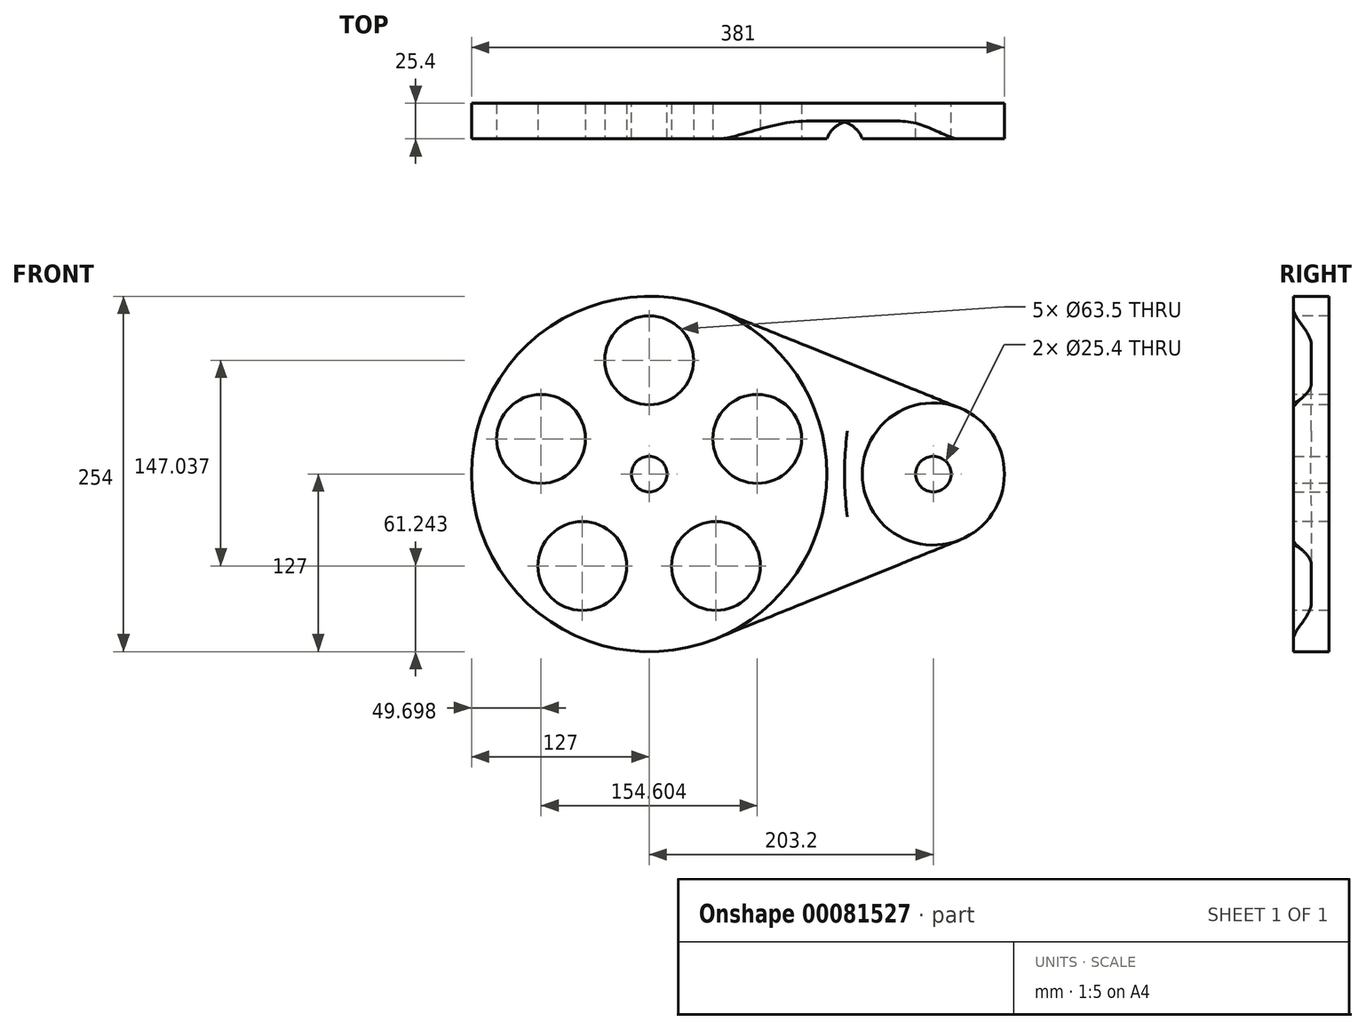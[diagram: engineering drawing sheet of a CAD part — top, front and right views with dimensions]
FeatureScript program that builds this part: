
annotation { "Feature Type Name" : "Feature", "Feature Type Description" : "" }
export const myFeature = defineFeature(function(context is Context, id is Id, definition is map)
    precondition{}
    {
        {
            var Q0;
            Q0=qCreatedBy(makeId("Front.planeOp"),FACE);
            var sketch = newSketch(context, id + "F0", { "sketchPlane" : qUnion([Q0])});
            skCircle(sketch, "E0", {"center": v(0, 0) * mm, "radius": 127 * mm});
            skCircle(sketch, "E1", {"center": v(203.2, 0) * mm, "radius": 50.8 * mm});
            skLineSegment(sketch, "E2", {"start": v(47.63, 117.73) * mm, "end": v(222.25, 47.1) * mm});
            skLineSegment(sketch, "E3", {"start": v(222.25, -47.1) * mm, "end": v(47.62, -117.73) * mm});
            skLineSegment(sketch, "E4", {"start": v(0, 0) * mm, "end": v(203.2, 0) * mm, "construction": true});
            skSolve(sketch);
        }
        {
            var Q0;
            {var subQ0=sQuery(id+"F0.wireOp",EDGE,"E0");var subQ1=makeQuery(id+"F0.imprint","INTERSECT",VERTEX,{"derivedFrom":[subQ0,sQuery(id+"F0.wireOp",EDGE,"E2")]});Q0=makeQuery(id+"F0.imprint","IMPRINT",FACE,{"disambiguationData":[TD([[makeQuery(id+"F0.imprint","IMPRINT",EDGE,{"disambiguationData":[TD([[subQ1,-1.0]])],"derivedFrom":subQ0}),1.0]])]});}
            var Q1;
            {var subQ0=sQuery(id+"F0.wireOp",EDGE,"E2");Q1=makeQuery(id+"F0.imprint","IMPRINT",FACE,{"disambiguationData":[TD([[makeQuery(id+"F0.imprint","IMPRINT",EDGE,{"derivedFrom":subQ0}),-1.0]])]});}
            var Q2;
            {var subQ0=sQuery(id+"F0.wireOp",EDGE,"E1");var subQ1=makeQuery(id+"F0.imprint","INTERSECT",VERTEX,{"derivedFrom":[subQ0,sQuery(id+"F0.wireOp",EDGE,"E2")]});Q2=makeQuery(id+"F0.imprint","IMPRINT",FACE,{"disambiguationData":[TD([[makeQuery(id+"F0.imprint","IMPRINT",EDGE,{"disambiguationData":[TD([[subQ1,-1.0]])],"derivedFrom":subQ0}),1.0]])]});}
            extrude(context, id + "F7", {"entities" : qUnion([Q0, Q1, Q2]), "depth" : 12.7 * mm});
        }
        {
            var Q0;
            {var subQ0=sQuery(id+"F0.wireOp",EDGE,"E0");var subQ1=makeQuery(id+"F0.imprint","INTERSECT",VERTEX,{"derivedFrom":[subQ0,sQuery(id+"F0.wireOp",EDGE,"E2")]});Q0=makeQuery(id+"F0.imprint","IMPRINT",FACE,{"disambiguationData":[TD([[makeQuery(id+"F0.imprint","IMPRINT",EDGE,{"disambiguationData":[TD([[subQ1,-1.0]])],"derivedFrom":subQ0}),1.0]])]});}
            var Q1;
            {var subQ0=sQuery(id+"F0.wireOp",EDGE,"E1");var subQ1=makeQuery(id+"F0.imprint","INTERSECT",VERTEX,{"derivedFrom":[subQ0,sQuery(id+"F0.wireOp",EDGE,"E2")]});Q1=makeQuery(id+"F0.imprint","IMPRINT",FACE,{"disambiguationData":[TD([[makeQuery(id+"F0.imprint","IMPRINT",EDGE,{"disambiguationData":[TD([[subQ1,-1.0]])],"derivedFrom":subQ0}),1.0]])]});}
            extrude(context, id + "F8", {"entities" : qUnion([Q0, Q1]), "operationType" : NewBodyOperationType.ADD, "depth" : 25.4 * mm});
        }
        {
            var Q0;
            {var subQ0=sQuery(id+"F0.wireOp",EDGE,"E0");var subQ1=makeQuery(id+"F0.imprint","INTERSECT",VERTEX,{"derivedFrom":[subQ0,sQuery(id+"F0.wireOp",EDGE,"E2")]});Q0=makeQuery(id+"F0.imprint","IMPRINT",FACE,{"disambiguationData":[TD([[makeQuery(id+"F0.imprint","IMPRINT",EDGE,{"disambiguationData":[TD([[subQ1,-1.0]])],"derivedFrom":subQ0}),1.0]])]});}
            var sketch = newSketch(context, id + "F9", { "sketchPlane" : qUnion([Q0])});
            skCircle(sketch, "E5", {"center": v(0, 0) * mm, "radius": 12.7 * mm});
            skCircle(sketch, "E6", {"center": v(203.2, 0) * mm, "radius": 12.7 * mm});
            skSolve(sketch);
        }
        {
            var Q0;
            Q0 = qSketchRegion(id + "F9", true);
            extrude(context, id + "F10", {"entities" : qUnion([Q0]), "operationType" : NewBodyOperationType.REMOVE, "endBound" : BoundingType.THROUGH_ALL, "depth" : 25.4 * mm});
        }
        {
            var Q0;
            {var subQ0=sQuery(id+"F0.wireOp",EDGE,"E0");Q0=makeQuery(id+"F8.boolean.opBoolean","INTERSECT",EDGE,{"derivedFrom":[makeQuery(id+"F7.opExtrude","CAP_FACE",FACE,{"disambiguationData":[OSD([subQ0,sQuery(id+"F0.wireOp",EDGE,"E1"),sQuery(id+"F0.wireOp",EDGE,"E2"),sQuery(id+"F0.wireOp",EDGE,"E3")])],"isStart":false}),makeQuery(id+"F8.opExtrude","SWEPT_FACE",FACE,{"disambiguationData":[OSD([subQ0])]})]});}
            var Q1;
            {var subQ0=sQuery(id+"F0.wireOp",EDGE,"E1");Q1=makeQuery(id+"F8.boolean.opBoolean","INTERSECT",EDGE,{"derivedFrom":[makeQuery(id+"F7.opExtrude","CAP_FACE",FACE,{"disambiguationData":[OSD([sQuery(id+"F0.wireOp",EDGE,"E0"),subQ0,sQuery(id+"F0.wireOp",EDGE,"E2"),sQuery(id+"F0.wireOp",EDGE,"E3")])],"isStart":false}),makeQuery(id+"F8.opExtrude","SWEPT_FACE",FACE,{"disambiguationData":[OSD([subQ0])]})]});}
            fillet(context, id + "F1", {"entities" : qUnion([Q0, Q1]), "radius" : 19.05 * mm, "tangentPropagation" : true, "allowEdgeOverflow" : false});
        }
        {
            var Q0;
            Q0=makeQuery(id+"F8.opExtrude","CAP_FACE",FACE,{"disambiguationData":[OSD([sQuery(id+"F0.wireOp",EDGE,"E0")])],"isStart":false});
            var sketch = newSketch(context, id + "F2", { "sketchPlane" : qUnion([Q0])});
            skCircle(sketch, "E7", {"center": v(0, 81.28) * mm, "radius": 31.75 * mm});
            skCircle(sketch, "E8.1.0", {"center": v(-77.3, 25.12) * mm, "radius": 31.75 * mm});
            skCircle(sketch, "E8.2.0", {"center": v(-47.78, -65.76) * mm, "radius": 31.75 * mm});
            skCircle(sketch, "E8.3.0", {"center": v(47.78, -65.76) * mm, "radius": 31.75 * mm});
            skCircle(sketch, "E8.4.0", {"center": v(77.3, 25.12) * mm, "radius": 31.75 * mm});
            skPoint(sketch, "E8.center", {"position": v(0, 0) * mm});
            skSolve(sketch);
        }
        {
            var Q0;
            Q0 = qSketchRegion(id + "F2", true);
            extrude(context, id + "F11", {"entities" : qUnion([Q0]), "operationType" : NewBodyOperationType.REMOVE, "endBound" : BoundingType.THROUGH_ALL, "oppositeDirection" : true, "depth" : 25.4 * mm});
        }
        {
            var Q0;
            Q0=makeQuery(id+"F8.opExtrude","CAP_FACE",FACE,{"disambiguationData":[OSD([sQuery(id+"F0.wireOp",EDGE,"E0")])],"isStart":false});
            var sketch = newSketch(context, id + "F3", { "sketchPlane" : qUnion([Q0])});
            skCircle(sketch, "E9", {"center": v(-84.55, -28.8) * mm, "radius": 27.78 * mm});
            skSolve(sketch);
        }
        {
            var Q0;
            Q0 = qSketchRegion(id + "F3", true);
            extrude(context, id + "F4", {"entities" : qUnion([Q0]), "depth" : 25.4 * mm});
        }
        {
            var Q0;
            Q0=makeQuery(id+"F4.opExtrude","SWEPT_BODY",BODY,{"disambiguationData":[OSD([sQuery(id+"F3.wireOp",EDGE,"E9")])]});
            deleteBodies(context, id + "F5", {"entities" : qUnion([Q0])});
        }
    });
